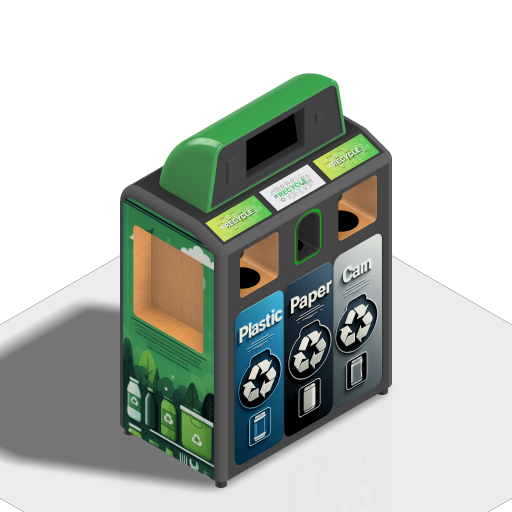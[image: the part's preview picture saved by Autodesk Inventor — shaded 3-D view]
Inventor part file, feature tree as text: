
AUTODESK INVENTOR PART (.ipt)
format: ipt  version: 2024.1 (Build 281209000, 209)  size: 2,277,888 bytes
history: native  units: mm
features: projected_geometry x24, sketch x20, extrude x16, other x16, plane x6, fillet x5, chamfer x1
ambient origin geometry x8: Origin, YZ Plane, XZ Plane, XY Plane, X Axis, Y Axis, Z Axis, Center Point
bodies: Solid1 (feature_tree)
feature tree (88):
  extrude  "Extrusion1"  Depth=40.0mm
  chamfer  "Chamfer1"  Distance=1200.0mm
  fillet  "Fillet1"  Radius=40.0mm
  extrude  "Extrusion2"  Depth=20.0mm
  extrude  "Extrusion3"  Depth=60.0mm
  extrude  "Extrusion4"  Depth=450.0mm
  fillet  "Fillet2"  Radius=100.0mm
  extrude  "Extrusion5"  Depth=200.0mm
  extrude  "Extrusion6"  Depth=50.0mm
  extrude  "Extrusion7"  Depth=10.0mm TaperAngle=0.0deg
  extrude  "Extrusion8"  Depth=2.5mm
  extrude  "Extrusion12"  Depth=2.5mm
  fillet  "Fillet3"  Radius=2.5mm
  fillet  "Fillet4"  Radius=5.0mm
  extrude  "Extrusion10"  Depth=40.0mm
  extrude  "Extrusion11"  Depth=40.0mm
  fillet  "Fillet5"  Radius=40.0mm
  extrude  "Extrusion13"  Depth=5.0mm
  extrude  "Extrusion14"  Depth=10.0mm TaperAngle=0.0deg
  extrude  "Extrusion15"  Depth=300.0mm TaperAngle=0.0deg
  plane  "Work Plane1"
  sketch  "Sketch18"  dims[d47=0.0mm d48=0.0mm d52=60.0mm]
  other  "Decal2"
  other  "Decal3"
  other  "Decal4"
  plane  "Work Plane2"
  plane  "Work Plane3"
  plane  "Work Plane4"
  other  "Decal7"
  other  "Decal8"
  plane  "Work Plane5"
  extrude  "Extrusion16"  Depth=60.0mm
  plane  "Work Plane6"
  sketch  "Sketch26"  dims[d61=80.0mm]
  other  "Decal10"
  other  "Decal11"
  other  "Decal12"
  extrude  "Extrusion17"  Depth=10.0mm TaperAngle=0.0deg
  sketch  "Sketch1"  dims[d0=600.0mm d1=1000.0mm d2=1200.0mm d3=0.0mm d5=40.0mm]
  sketch  "Sketch3"  dims[d6=60.0mm d7=2.0mm d8=12.217305mm d9=20.0mm]
  projected_geometry  "Projected Loop1"
  sketch  "Sketch4"  dims[d10=60.0mm d11=60.0mm]
  projected_geometry  "Projected Loop2"
  sketch  "Sketch5"  dims[d12=120.0mm d13=450.0mm d14=100.0mm d15=0.0mm]
  projected_geometry  "Projected Loop3"
  sketch  "Sketch6"  dims[d16=150.0mm d17=200.0mm]
  projected_geometry  "Projected Loop4"
  sketch  "Sketch7"  dims[d18=120.0mm d19=50.0mm]
  projected_geometry  "Projected Loop5"
  sketch  "Sketch8"  dims[d20=10.0mm d21=200.0mm d22=0.0mm]
  projected_geometry  "Projected Loop6"
  sketch  "Sketch9"  dims[d23=800.0mm d26=2.5mm]
  projected_geometry  "Projected Loop7"
  sketch  "Sketch11"  dims[d27=2.5mm d28=2.5mm d29=2.5mm d30=5.0mm]
  projected_geometry  "Projected Loop9"
  sketch  "Sketch12"  dims[d31=5.0mm d32=0.0mm d33=40.0mm]
  projected_geometry  "Projected Loop10"
  sketch  "Sketch13"  dims[d34=280.0mm d35=5.0mm d36=40.0mm]
  projected_geometry  "Projected Loop11"
  projected_geometry  "Projected Loop12"
  projected_geometry  "Projected Loop13"
  sketch  "Sketch14"  dims[d37=20.0mm d38=5.0mm]
  projected_geometry  "Projected Loop15"
  sketch  "Sketch15"  dims[d39=5.0mm d40=0.0mm d41=10.0mm d42=0.0mm]
  projected_geometry  "Projected Loop16"
  projected_geometry  "Projected Loop17"
  sketch  "Sketch16"  dims[d43=800.0mm d45=300.0mm d46=0.0mm]
  projected_geometry  "Projected Loop18"
  projected_geometry  "Projected Loop19"
  projected_geometry  "Projected Loop20"
  projected_geometry  "Projected Loop21"
  projected_geometry  "Projected Loop22"
  other  "Image1"
  other  "Image2"
  other  "Image3"
  sketch  "Sketch21"  dims[d53=10.0mm d55=332.0mm d56=0.0mm]
  projected_geometry  "Projected Loop24"
  other  "Image6"
  sketch  "Sketch22"  dims[d59=50.0mm]
  other  "Image7"
  projected_geometry  "Projected Loop25"
  sketch  "Sketch25"  dims[d60=190.0mm]
  projected_geometry  "Projected Loop26"
  other  "Image10"
  other  "Image12"
  other  "Image13"
  sketch  "Sketch27"  dims[d62=17.453293mm d63=80.0mm d64=6.0mm d65=15.0mm d66=40.0mm d68=20.0mm d69=10.0mm d71=10.0mm d73=20.0mm d74=20.0mm d75=5.0mm d76=60.0mm d77=3.0mm d78=10.0mm d79=0.0mm d80=100.0mm d81=340.0mm d82=50.0mm d84=50.0mm d85=0.0mm d86=0.0mm d87=5.0mm d88=5.0mm d89=5.0mm d90=30.0mm d91=20.0mm d92=260.0mm d93=840.0mm d94=5.0mm d95=30.0mm d96=200.0mm d97=200.0mm d98=35.0mm d99=30.0mm d100=30.0mm d101=30.0mm d102=5.0mm d103=0.0mm d104=20.0mm d105=230.0mm d106=220.0mm d107=200.0mm d108=0.0mm d109=150.0mm d110=10.0mm d111=0.0mm d112=100.0mm d142=755.0mm d159=755.0mm d192=100.0mm d200=309.0mm d215=425.0mm d217=520.0mm d226=520.0mm d243=747.75mm d257=10.0mm d258=10.0mm d259=0.0mm d260=121.0mm d325=115.0mm d338=115.0mm d343=115.0mm d355=50.0mm d356=40.0mm d357=0.0mm d244=0.0mm d245=0.0mm d246=0.0mm]
  projected_geometry  "Projected Loop27"
